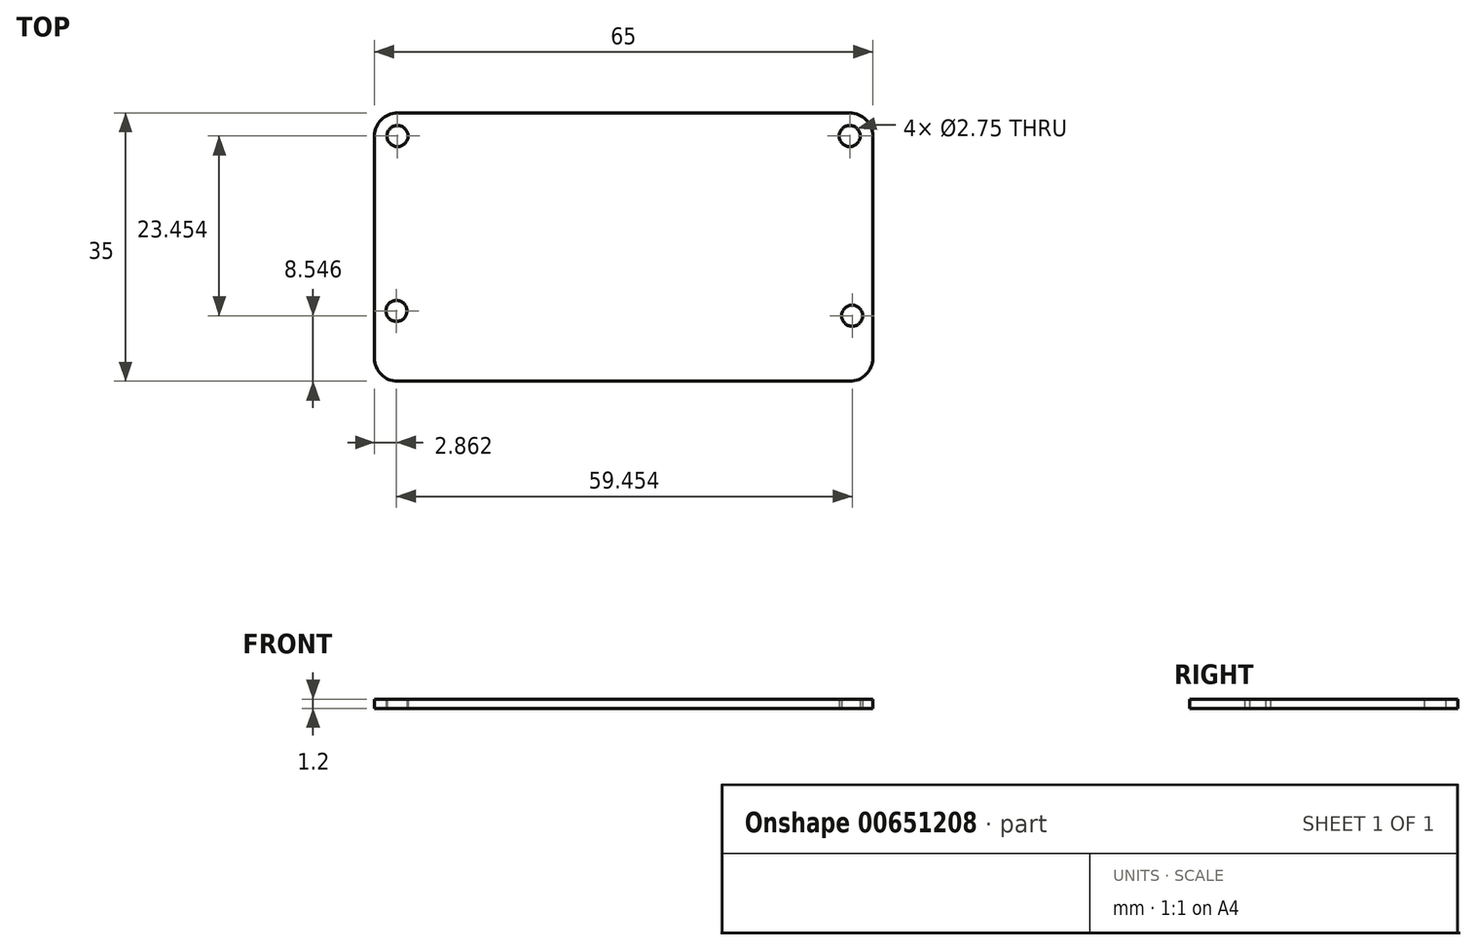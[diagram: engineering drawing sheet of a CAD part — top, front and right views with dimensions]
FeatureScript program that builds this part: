
annotation { "Feature Type Name" : "Feature", "Feature Type Description" : "" }
export const myFeature = defineFeature(function(context is Context, id is Id, definition is map)
    precondition{}
    {
        {
            var Q0;
            Q0=qCreatedBy(makeId("Top.planeOp"),FACE);
            var sketch = newSketch(context, id + "F0", { "sketchPlane" : qUnion([Q0])});
            skLineSegment(sketch, "E0.bottom", {"start": v(-29.5, 17.5) * mm, "end": v(29.5, 17.5) * mm});
            skLineSegment(sketch, "E0.top", {"start": v(-29.5, -17.5) * mm, "end": v(29.5, -17.5) * mm});
            skLineSegment(sketch, "E0.left", {"start": v(-32.5, 14.5) * mm, "end": v(-32.5, -14.5) * mm});
            skLineSegment(sketch, "E0.right", {"start": v(32.5, 14.5) * mm, "end": v(32.5, -14.5) * mm});
            skPoint(sketch, "E0.middle", {"position": v(0, 0) * mm});
            skPoint(sketch, "E1.visualSharp", {"position": v(-32.5, 17.5) * mm});
            skArc(sketch, "E1.filletArc", {"start": v(-29.5, 17.5) * mm, "mid": v(-31.62, 16.62) * mm, "end": v(-32.5, 14.5) * mm});
            skPoint(sketch, "E2.visualSharp", {"position": v(32.5, 17.5) * mm});
            skArc(sketch, "E2.filletArc", {"start": v(32.5, 14.5) * mm, "mid": v(31.62, 16.62) * mm, "end": v(29.5, 17.5) * mm});
            skPoint(sketch, "E3.visualSharp", {"position": v(32.5, -17.5) * mm});
            skArc(sketch, "E3.filletArc", {"start": v(29.5, -17.5) * mm, "mid": v(31.62, -16.62) * mm, "end": v(32.5, -14.5) * mm});
            skPoint(sketch, "E4.visualSharp", {"position": v(-32.5, -17.5) * mm});
            skArc(sketch, "E4.filletArc", {"start": v(-32.5, -14.5) * mm, "mid": v(-31.62, -16.62) * mm, "end": v(-29.5, -17.5) * mm});
            skCircle(sketch, "E5", {"center": v(-29.5, 14.5) * mm, "radius": 1.38 * mm});
            skCircle(sketch, "E6", {"center": v(29.5, 14.5) * mm, "radius": 1.38 * mm});
            skCircle(sketch, "E7", {"center": v(-29.64, -8.33) * mm, "radius": 1.38 * mm});
            skCircle(sketch, "E8", {"center": v(29.82, -8.95) * mm, "radius": 1.38 * mm});
            skSolve(sketch);
        }
        {
            var Q0;
            Q0=makeQuery(id+"F0.imprint","IMPRINT",FACE,{"disambiguationData":[TD([[makeQuery(id+"F0.imprint","IMPRINT",EDGE,{"derivedFrom":sQuery(id+"F0.wireOp",EDGE,"E0.bottom")}),-1.0]])]});
            extrude(context, id + "F1", {"entities" : qUnion([Q0]), "depth" : 1.2 * mm, "offsetDistance" : 25 * mm});
        }
    });
